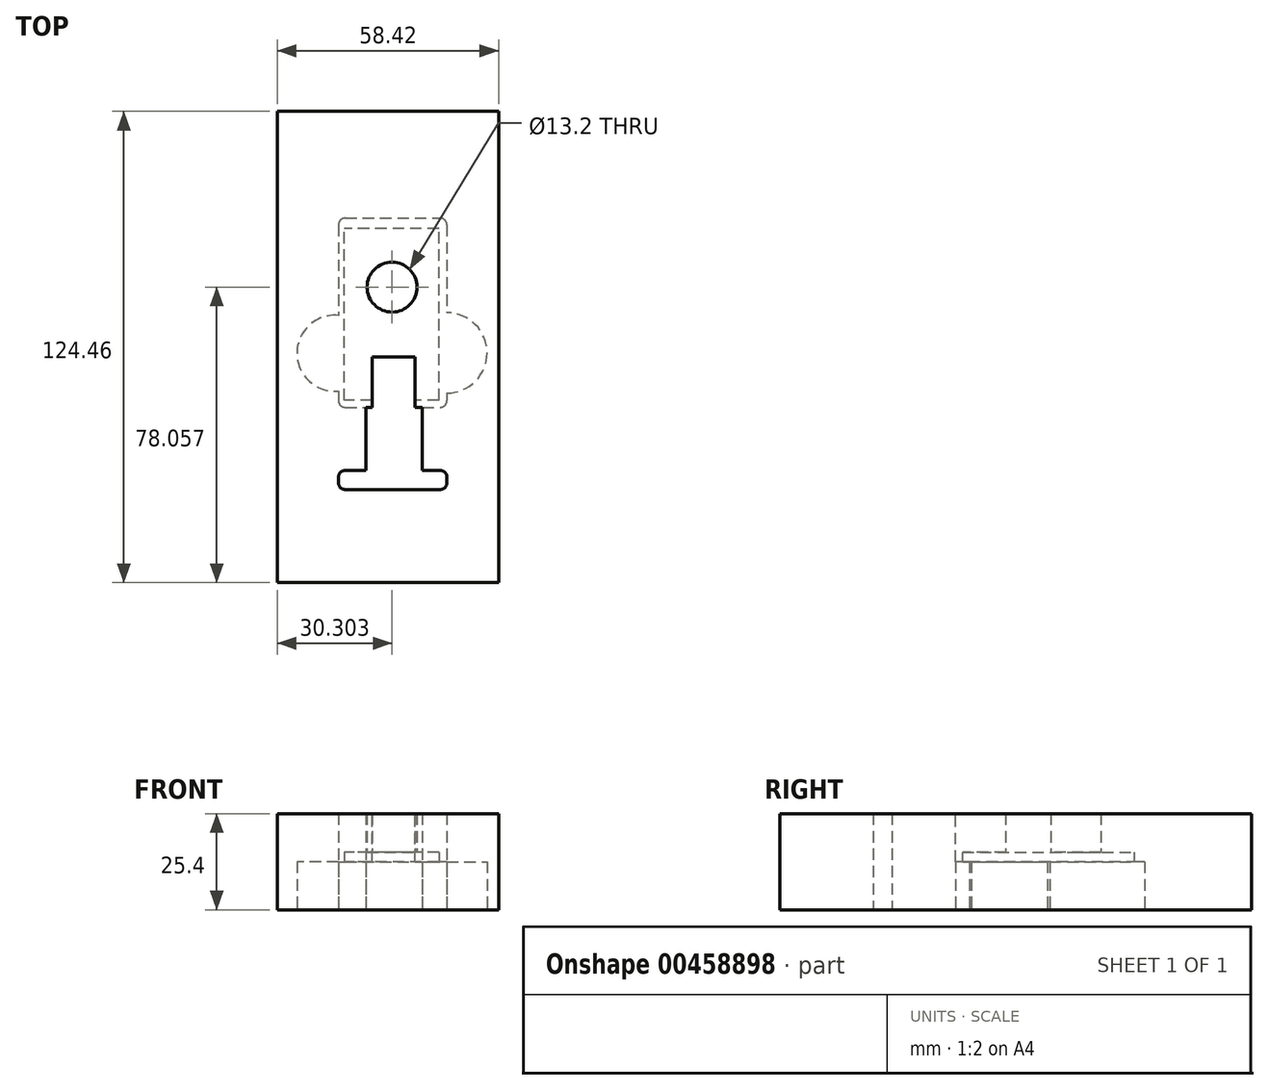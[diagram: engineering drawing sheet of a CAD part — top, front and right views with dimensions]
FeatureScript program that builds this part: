
annotation { "Feature Type Name" : "Feature", "Feature Type Description" : "" }
export const myFeature = defineFeature(function(context is Context, id is Id, definition is map)
    precondition{}
    {
        {
            var Q0;
            Q0=qCreatedBy(makeId("Top.planeOp"),FACE);
            var sketch = newSketch(context, id + "F0", { "sketchPlane" : qUnion([Q0])});
            skLineSegment(sketch, "E0.bottom", {"start": v(-47.75, 64.85) * mm, "end": v(10.67, 64.85) * mm});
            skLineSegment(sketch, "E0.top", {"start": v(-47.75, -59.6) * mm, "end": v(10.67, -59.6) * mm});
            skLineSegment(sketch, "E0.left", {"start": v(-47.75, 64.85) * mm, "end": v(-47.75, -59.6) * mm});
            skLineSegment(sketch, "E0.right", {"start": v(10.67, 64.85) * mm, "end": v(10.67, -59.6) * mm});
            skSolve(sketch);
        }
        {
            var Q0;
            Q0 = qSketchRegion(id + "F0", true);
            extrude(context, id + "F1", {"entities" : qUnion([Q0]), "depth" : 25.4 * mm, "offsetDistance" : 25.4 * mm});
        }
        {
            var Q0;
            Q0=qCreatedBy(makeId("Top.planeOp"),FACE);
            var sketch = newSketch(context, id + "F2", { "sketchPlane" : qUnion([Q0])});
            skLineSegment(sketch, "E1.bottom", {"start": v(-31.59, 36.66) * mm, "end": v(-2.99, 36.66) * mm});
            skLineSegment(sketch, "E1.top", {"start": v(-31.59, -13.3) * mm, "end": v(-24.35, -13.3) * mm});
            skLineSegment(sketch, "E1.left", {"start": v(-31.59, 36.66) * mm, "end": v(-31.59, -13.3) * mm});
            skLineSegment(sketch, "E1.right", {"start": v(-2.99, 36.66) * mm, "end": v(-2.99, -13.3) * mm});
            skLineSegment(sketch, "E2.left", {"start": v(-24.35, -13.3) * mm, "end": v(-24.35, -29.96) * mm});
            skLineSegment(sketch, "E2.right", {"start": v(-9.44, -13.3) * mm, "end": v(-9.44, -29.96) * mm});
            skLineSegment(sketch, "E3.bottom", {"start": v(-31.59, -29.96) * mm, "end": v(-24.35, -29.96) * mm});
            skLineSegment(sketch, "E3.top", {"start": v(-31.59, -35.03) * mm, "end": v(-2.99, -35.03) * mm});
            skLineSegment(sketch, "E3.left", {"start": v(-31.59, -29.96) * mm, "end": v(-31.59, -35.03) * mm});
            skLineSegment(sketch, "E3.right", {"start": v(-2.99, -29.96) * mm, "end": v(-2.99, -35.03) * mm});
            skLineSegment(sketch, "E4.trimOffspring", {"start": v(-9.44, -13.3) * mm, "end": v(-2.99, -13.3) * mm});
            skLineSegment(sketch, "E5.trimOffspring", {"start": v(-9.44, -29.96) * mm, "end": v(-2.99, -29.96) * mm});
            skLineSegment(sketch, "E6", {"start": v(-9.44, -13.3) * mm, "end": v(-24.35, -13.3) * mm});
            skLineSegment(sketch, "E7", {"start": v(-9.44, -29.96) * mm, "end": v(-24.35, -29.96) * mm});
            skSolve(sketch);
        }
        {
            var Q0;
            Q0=makeQuery(id+"F2.imprint","IMPRINT",FACE,{"disambiguationData":[TD([[makeQuery(id+"F2.imprint","IMPRINT",EDGE,{"derivedFrom":sQuery(id+"F2.wireOp",EDGE,"E1.bottom")}),-1.0]])]});
            extrude(context, id + "F3", {"entities" : qUnion([Q0]), "operationType" : NewBodyOperationType.REMOVE, "depth" : 12.7 * mm, "offsetDistance" : 25.4 * mm});
        }
        {
            var Q0;
            Q0=makeQuery(id+"F2.imprint","IMPRINT",FACE,{"disambiguationData":[TD([[makeQuery(id+"F2.imprint","IMPRINT",EDGE,{"derivedFrom":sQuery(id+"F2.wireOp",EDGE,"E2.left")}),1.0]])]});
            extrude(context, id + "F4", {"entities" : qUnion([Q0]), "operationType" : NewBodyOperationType.REMOVE, "endBound" : BoundingType.THROUGH_ALL, "depth" : 15.24 * mm, "offsetDistance" : 25.4 * mm});
        }
        {
            var Q0;
            Q0=makeQuery(id+"F2.imprint","IMPRINT",FACE,{"disambiguationData":[TD([[makeQuery(id+"F2.imprint","IMPRINT",EDGE,{"derivedFrom":sQuery(id+"F2.wireOp",EDGE,"E3.bottom")}),-1.0]])]});
            extrude(context, id + "F5", {"entities" : qUnion([Q0]), "operationType" : NewBodyOperationType.REMOVE, "endBound" : BoundingType.THROUGH_ALL, "depth" : 20.32 * mm, "offsetDistance" : 25.4 * mm});
        }
        {
            var Q0;
            Q0=makeQuery(id+"F5.boolean.opBoolean","COPY",EDGE,{"derivedFrom":makeQuery(id+"F5.opExtrude","SWEPT_EDGE",EDGE,{"disambiguationData":[OSD([sQuery(id+"F2.wireOp",EDGE,"E3.top"),sQuery(id+"F2.wireOp",EDGE,"E3.right")])]})});
            var Q1;
            Q1=makeQuery(id+"F3.boolean.opBoolean","COPY",EDGE,{"derivedFrom":makeQuery(id+"F3.opExtrude","SWEPT_EDGE",EDGE,{"disambiguationData":[OSD([sQuery(id+"F2.wireOp",EDGE,"E1.right"),sQuery(id+"F2.wireOp",EDGE,"E4.trimOffspring")])]})});
            var Q2;
            Q2=makeQuery(id+"F5.boolean.opBoolean","COPY",EDGE,{"derivedFrom":makeQuery(id+"F5.opExtrude","SWEPT_EDGE",EDGE,{"disambiguationData":[OSD([sQuery(id+"F2.wireOp",EDGE,"E3.right"),sQuery(id+"F2.wireOp",EDGE,"E5.trimOffspring")])]})});
            var Q3;
            Q3=makeQuery(id+"F3.boolean.opBoolean","COPY",EDGE,{"derivedFrom":makeQuery(id+"F3.opExtrude","SWEPT_EDGE",EDGE,{"disambiguationData":[OSD([sQuery(id+"F2.wireOp",EDGE,"E1.bottom"),sQuery(id+"F2.wireOp",EDGE,"E1.right")])]})});
            var Q4;
            Q4=makeQuery(id+"F3.boolean.opBoolean","COPY",EDGE,{"derivedFrom":makeQuery(id+"F3.opExtrude","SWEPT_EDGE",EDGE,{"disambiguationData":[OSD([sQuery(id+"F2.wireOp",EDGE,"E1.bottom"),sQuery(id+"F2.wireOp",EDGE,"E1.left")])]})});
            var Q5;
            Q5=makeQuery(id+"F3.boolean.opBoolean","COPY",EDGE,{"derivedFrom":makeQuery(id+"F3.opExtrude","SWEPT_EDGE",EDGE,{"disambiguationData":[OSD([sQuery(id+"F2.wireOp",EDGE,"E1.top"),sQuery(id+"F2.wireOp",EDGE,"E1.left")])]})});
            var Q6;
            Q6=makeQuery(id+"F5.boolean.opBoolean","COPY",EDGE,{"derivedFrom":makeQuery(id+"F5.opExtrude","SWEPT_EDGE",EDGE,{"disambiguationData":[OSD([sQuery(id+"F2.wireOp",EDGE,"E3.bottom"),sQuery(id+"F2.wireOp",EDGE,"E3.left")])]})});
            var Q7;
            Q7=makeQuery(id+"F5.boolean.opBoolean","COPY",EDGE,{"derivedFrom":makeQuery(id+"F5.opExtrude","SWEPT_EDGE",EDGE,{"disambiguationData":[OSD([sQuery(id+"F2.wireOp",EDGE,"E3.top"),sQuery(id+"F2.wireOp",EDGE,"E3.left")])]})});
            fillet(context, id + "F6", {"entities" : qUnion([Q0, Q1, Q2, Q3, Q4, Q5, Q6, Q7]), "radius" : 1.78 * mm, "tangentPropagation" : true, "allowEdgeOverflow" : false});
        }
        {
            var Q0;
            Q0=makeQuery(id+"F1.opExtrude","CAP_FACE",FACE,{"disambiguationData":[OSD([sQuery(id+"F0.wireOp",EDGE,"E0.bottom"),sQuery(id+"F0.wireOp",EDGE,"E0.top"),sQuery(id+"F0.wireOp",EDGE,"E0.left"),sQuery(id+"F0.wireOp",EDGE,"E0.right")])],"isStart":true});
            var sketch = newSketch(context, id + "F7", { "sketchPlane" : qUnion([Q0])});
            skArc(sketch, "E8", {"start": v(-31.59, 9.02) * mm, "mid": v(-42.56, -0.97) * mm, "end": v(-31.59, -10.97) * mm});
            skArc(sketch, "E9", {"start": v(-2.99, -11.68) * mm, "mid": v(7.63, -1.06) * mm, "end": v(-2.99, 9.55) * mm});
            skLineSegment(sketch, "E10", {"start": v(-2.99, -11.68) * mm, "end": v(-2.99, 9.55) * mm});
            skLineSegment(sketch, "E11", {"start": v(-31.59, -10.97) * mm, "end": v(-31.59, 9.02) * mm});
            skPoint(sketch, "E12", {"position": v(-31.59, -11.68) * mm});
            skSolve(sketch);
        }
        {
            var Q0;
            Q0 = qSketchRegion(id + "F7", true);
            extrude(context, id + "F8", {"entities" : qUnion([Q0]), "operationType" : NewBodyOperationType.REMOVE, "oppositeDirection" : true, "depth" : 12.7 * mm, "offsetDistance" : 25.4 * mm});
        }
        {
            var Q0;
            Q0=makeQuery(id+"F8.boolean.opBoolean","MERGE",FACE,{"derivedFrom":[makeQuery(id+"F3.boolean.opBoolean","COPY",FACE,{"derivedFrom":makeQuery(id+"F3.opExtrude","CAP_FACE",FACE,{"disambiguationData":[OSD([sQuery(id+"F2.wireOp",EDGE,"E1.bottom"),sQuery(id+"F2.wireOp",EDGE,"E1.top"),sQuery(id+"F2.wireOp",EDGE,"E1.left"),sQuery(id+"F2.wireOp",EDGE,"E1.right"),sQuery(id+"F2.wireOp",EDGE,"E4.trimOffspring"),sQuery(id+"F2.wireOp",EDGE,"E6")])],"isStart":false})}),makeQuery(id+"F8.opExtrude","CAP_FACE",FACE,{"disambiguationData":[OSD([sQuery(id+"F7.wireOp",EDGE,"E8"),sQuery(id+"F7.wireOp",EDGE,"E11")])],"isStart":false}),makeQuery(id+"F8.opExtrude","CAP_FACE",FACE,{"disambiguationData":[OSD([sQuery(id+"F7.wireOp",EDGE,"E9"),sQuery(id+"F7.wireOp",EDGE,"E10")])],"isStart":false})]});
            var sketch = newSketch(context, id + "F9", { "sketchPlane" : qUnion([Q0])});
            skCircle(sketch, "E13", {"center": v(-17.45, -18.45) * mm, "radius": 6.6 * mm});
            skSolve(sketch);
        }
        {
            var Q0;
            Q0 = qSketchRegion(id + "F9", true);
            extrude(context, id + "F10", {"entities" : qUnion([Q0]), "operationType" : NewBodyOperationType.REMOVE, "endBound" : BoundingType.THROUGH_ALL, "oppositeDirection" : true, "depth" : 25.4 * mm, "offsetDistance" : 25.4 * mm});
        }
        {
            var Q0;
            Q0=makeQuery(id+"F8.boolean.opBoolean","MERGE",FACE,{"derivedFrom":[makeQuery(id+"F3.boolean.opBoolean","COPY",FACE,{"derivedFrom":makeQuery(id+"F3.opExtrude","CAP_FACE",FACE,{"disambiguationData":[OSD([sQuery(id+"F2.wireOp",EDGE,"E1.bottom"),sQuery(id+"F2.wireOp",EDGE,"E1.top"),sQuery(id+"F2.wireOp",EDGE,"E1.left"),sQuery(id+"F2.wireOp",EDGE,"E1.right"),sQuery(id+"F2.wireOp",EDGE,"E4.trimOffspring"),sQuery(id+"F2.wireOp",EDGE,"E6")])],"isStart":false})}),makeQuery(id+"F8.opExtrude","CAP_FACE",FACE,{"disambiguationData":[OSD([sQuery(id+"F7.wireOp",EDGE,"E8"),sQuery(id+"F7.wireOp",EDGE,"E11")])],"isStart":false}),makeQuery(id+"F8.opExtrude","CAP_FACE",FACE,{"disambiguationData":[OSD([sQuery(id+"F7.wireOp",EDGE,"E9"),sQuery(id+"F7.wireOp",EDGE,"E10")])],"isStart":false})]});
            var sketch = newSketch(context, id + "F11", { "sketchPlane" : qUnion([Q0])});
            skSolve(sketch);
        }
        {
            var Q0;
            {var subQ9=sQuery(id+"F2.wireOp",EDGE,"E1.bottom");Q0=makeQuery(id+"F11.imprint","IMPRINT",FACE,{"disambiguationData":[TD([[makeQuery(id+"F11.imprint","IMPRINT",EDGE,{"derivedFrom":makeQuery(id+"F3.boolean.opBoolean","COPY",EDGE,{"derivedFrom":makeQuery(id+"F3.opExtrude","CAP_EDGE",EDGE,{"disambiguationData":[OSD([subQ9])],"isStart":false})})}),1.0]])]});}
            var sketch = newSketch(context, id + "F12", { "sketchPlane" : qUnion([Q0])});
            skLineSegment(sketch, "E14.bottom", {"start": v(-5.09, 11.4) * mm, "end": v(-30.04, 11.4) * mm});
            skLineSegment(sketch, "E14.top", {"start": v(-5.09, -33.9) * mm, "end": v(-30.04, -33.9) * mm});
            skLineSegment(sketch, "E14.left", {"start": v(-5.09, 11.4) * mm, "end": v(-5.09, -33.9) * mm});
            skLineSegment(sketch, "E14.right", {"start": v(-30.04, 11.4) * mm, "end": v(-30.04, -33.9) * mm});
            skSolve(sketch);
        }
        {
            var Q0;
            Q0 = qSketchRegion(id + "F12", true);
            extrude(context, id + "F13", {"entities" : qUnion([Q0]), "operationType" : NewBodyOperationType.REMOVE, "oppositeDirection" : true, "depth" : 2.54 * mm, "offsetDistance" : 25.4 * mm});
        }
        {
            var Q0;
            {var subQ9=sQuery(id+"F2.wireOp",EDGE,"E1.bottom");Q0=makeQuery(id+"F11.imprint","IMPRINT",FACE,{"disambiguationData":[TD([[makeQuery(id+"F11.imprint","IMPRINT",EDGE,{"derivedFrom":makeQuery(id+"F3.boolean.opBoolean","COPY",EDGE,{"derivedFrom":makeQuery(id+"F3.opExtrude","CAP_EDGE",EDGE,{"disambiguationData":[OSD([subQ9])],"isStart":false})})}),1.0]])]});}
            var sketch = newSketch(context, id + "F14", { "sketchPlane" : qUnion([Q0])});
            skLineSegment(sketch, "E15.bottom", {"start": v(-11.43, 0) * mm, "end": v(-22.75, 0) * mm});
            skLineSegment(sketch, "E15.top", {"start": v(-11.43, 17.16) * mm, "end": v(-22.75, 17.16) * mm});
            skLineSegment(sketch, "E15.left", {"start": v(-11.43, 0) * mm, "end": v(-11.43, 17.16) * mm});
            skLineSegment(sketch, "E15.right", {"start": v(-22.75, 0) * mm, "end": v(-22.75, 17.16) * mm});
            skSolve(sketch);
        }
        {
            var Q0;
            Q0 = qSketchRegion(id + "F14", true);
            extrude(context, id + "F15", {"entities" : qUnion([Q0]), "operationType" : NewBodyOperationType.REMOVE, "endBound" : BoundingType.THROUGH_ALL, "oppositeDirection" : true, "depth" : 25.4 * mm, "offsetDistance" : 25.4 * mm});
        }
    });
